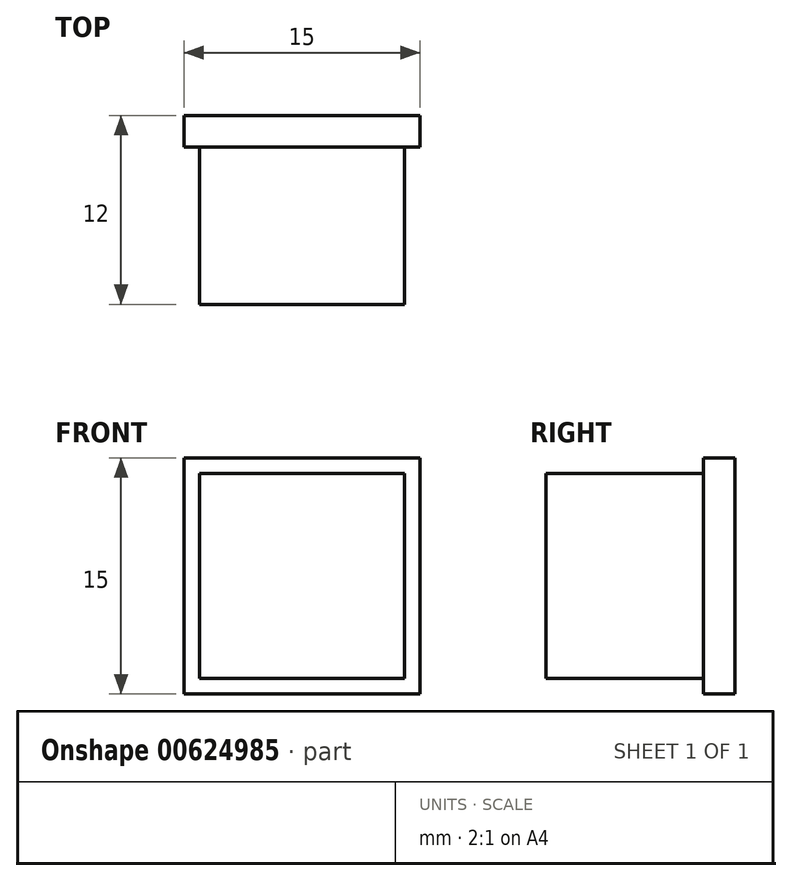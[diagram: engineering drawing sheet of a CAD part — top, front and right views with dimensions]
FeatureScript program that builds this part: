
annotation { "Feature Type Name" : "Feature", "Feature Type Description" : "" }
export const myFeature = defineFeature(function(context is Context, id is Id, definition is map)
    precondition{}
    {
        {
            var Q0;
            Q0=qCreatedBy(makeId("Front.planeOp"),FACE);
            var sketch = newSketch(context, id + "F0", { "sketchPlane" : qUnion([Q0])});
            skLineSegment(sketch, "E0.bottom", {"start": v(7.5, -7.5) * mm, "end": v(-7.5, -7.5) * mm});
            skLineSegment(sketch, "E0.top", {"start": v(7.5, 7.5) * mm, "end": v(-7.5, 7.5) * mm});
            skLineSegment(sketch, "E0.left", {"start": v(7.5, -7.5) * mm, "end": v(7.5, 7.5) * mm});
            skLineSegment(sketch, "E0.right", {"start": v(-7.5, -7.5) * mm, "end": v(-7.5, 7.5) * mm});
            skPoint(sketch, "E0.middle", {"position": v(0, 0) * mm});
            skSolve(sketch);
        }
        {
            var Q0;
            Q0=makeQuery(id+"F0.imprint","IMPRINT",FACE,{"disambiguationData":[TD([[makeQuery(id+"F0.imprint","IMPRINT",EDGE,{"derivedFrom":sQuery(id+"F0.wireOp",EDGE,"E0.bottom")}),-1.0]])]});
            extrude(context, id + "F1", {"entities" : qUnion([Q0]), "depth" : 2 * mm, "offsetDistance" : 25 * mm});
        }
        {
            var Q0;
            Q0=makeQuery(id+"F1.opExtrude","CAP_FACE",FACE,{"disambiguationData":[OSD([sQuery(id+"F0.wireOp",EDGE,"E0.bottom"),sQuery(id+"F0.wireOp",EDGE,"E0.top"),sQuery(id+"F0.wireOp",EDGE,"E0.left"),sQuery(id+"F0.wireOp",EDGE,"E0.right")])],"isStart":false});
            var sketch = newSketch(context, id + "F2", { "sketchPlane" : qUnion([Q0])});
            skLineSegment(sketch, "E1.0.0", {"start": v(7.5, -7.5) * mm, "end": v(7.5, 7.5) * mm});
            skLineSegment(sketch, "E1.0.1", {"start": v(7.5, 7.5) * mm, "end": v(-7.5, 7.5) * mm});
            skLineSegment(sketch, "E1.0.2", {"start": v(-7.5, 7.5) * mm, "end": v(-7.5, -7.5) * mm});
            skLineSegment(sketch, "E1.0.3", {"start": v(-7.5, -7.5) * mm, "end": v(7.5, -7.5) * mm});
            skLineSegment(sketch, "E2.0", {"start": v(6.5, -6.5) * mm, "end": v(6.5, 6.5) * mm});
            skLineSegment(sketch, "E2.1", {"start": v(-6.5, -6.5) * mm, "end": v(6.5, -6.5) * mm});
            skLineSegment(sketch, "E2.2", {"start": v(-6.5, 6.5) * mm, "end": v(-6.5, -6.5) * mm});
            skLineSegment(sketch, "E2.3", {"start": v(6.5, 6.5) * mm, "end": v(-6.5, 6.5) * mm});
            skSolve(sketch);
        }
        {
            var Q0;
            Q0=makeQuery(id+"F2.imprint","IMPRINT",FACE,{"disambiguationData":[TD([[makeQuery(id+"F2.imprint","IMPRINT",EDGE,{"derivedFrom":sQuery(id+"F2.wireOp",EDGE,"E2.0")}),1.0]])]});
            extrude(context, id + "F3", {"entities" : qUnion([Q0]), "operationType" : NewBodyOperationType.ADD, "depth" : 10 * mm, "offsetDistance" : 25 * mm});
        }
    });
